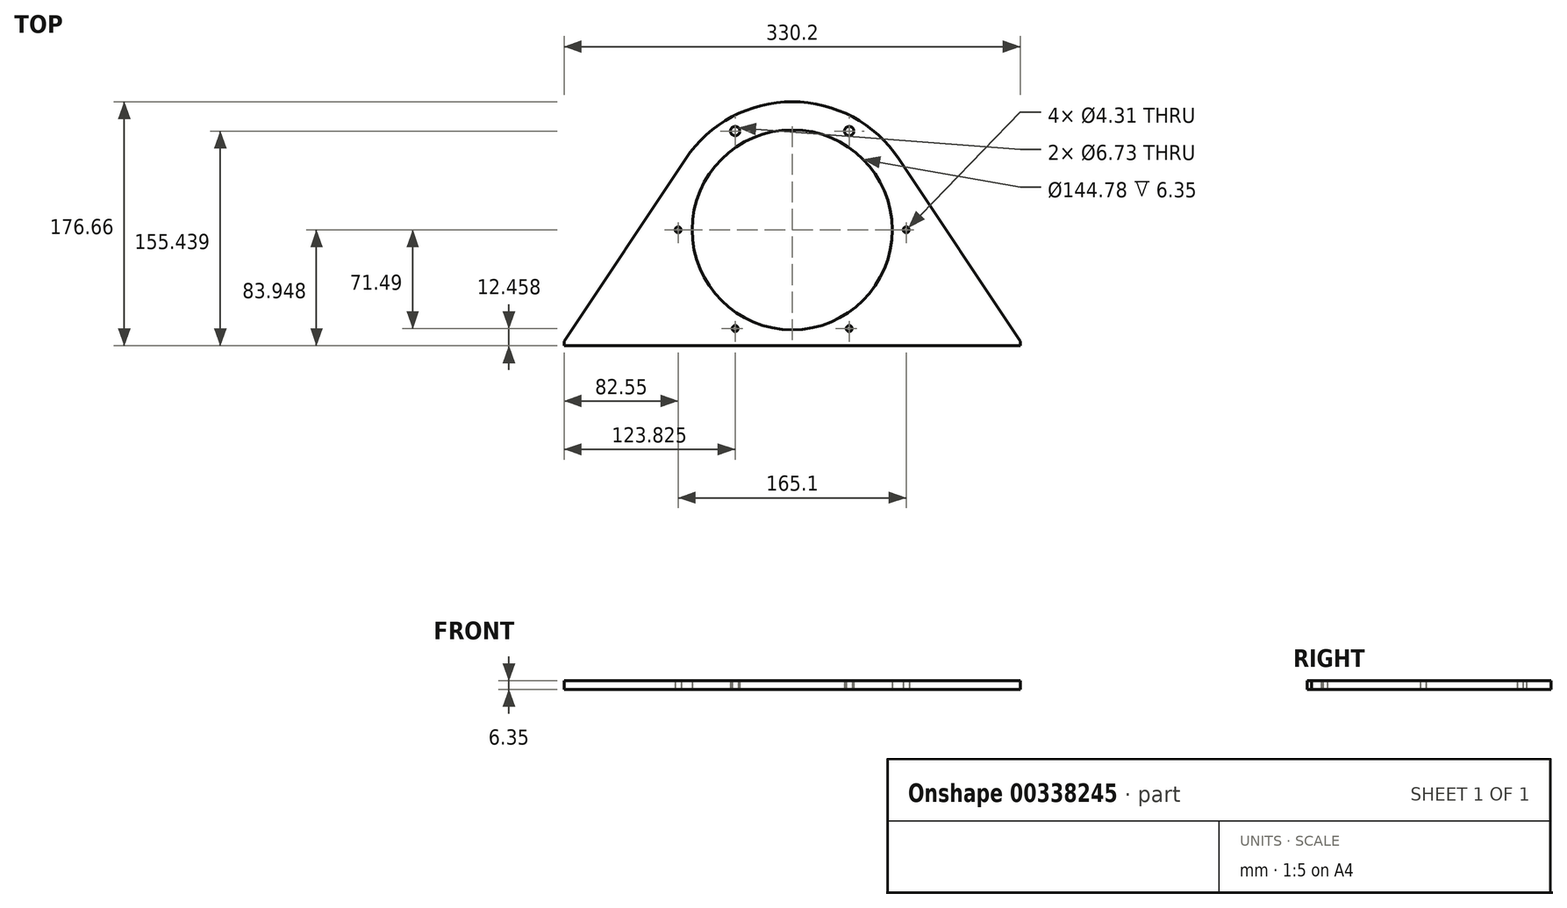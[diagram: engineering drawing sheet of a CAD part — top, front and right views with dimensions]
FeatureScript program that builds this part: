
annotation { "Feature Type Name" : "Feature", "Feature Type Description" : "" }
export const myFeature = defineFeature(function(context is Context, id is Id, definition is map)
    precondition{}
    {
        {
            var Q0;
            Q0=qCreatedBy(makeId("Top.planeOp"),FACE);
            var sketch = newSketch(context, id + "F0", { "sketchPlane" : qUnion([Q0])});
            skLineSegment(sketch, "E0", {"start": v(0, 0) * mm, "end": v(330.2, 0) * mm});
            skLineSegment(sketch, "E1", {"start": v(330.2, 0) * mm, "end": v(330.2, 3.17) * mm});
            skLineSegment(sketch, "E2", {"start": v(330.2, 3.17) * mm, "end": v(242.29, 135.3) * mm});
            skLineSegment(sketch, "E3", {"start": v(165.1, 0) * mm, "end": v(165.1, 83.95) * mm, "construction": true});
            skCircle(sketch, "E4", {"center": v(165.1, 83.95) * mm, "radius": 72.4 * mm});
            skArc(sketch, "E5", {"start": v(242.29, 135.3) * mm, "mid": v(165.1, 176.66) * mm, "end": v(87.91, 135.3) * mm});
            skLineSegment(sketch, "E6", {"start": v(165.1, 83.95) * mm, "end": v(247.65, 83.95) * mm, "construction": true});
            skLineSegment(sketch, "E7", {"start": v(165.1, 83.95) * mm, "end": v(123.82, 155.44) * mm, "construction": true});
            skLineSegment(sketch, "E8", {"start": v(165.1, 83.95) * mm, "end": v(206.38, 155.44) * mm, "construction": true});
            skLineSegment(sketch, "E9", {"start": v(165.1, 83.95) * mm, "end": v(165.1, 155.44) * mm, "construction": true});
            skLineSegment(sketch, "E10", {"start": v(123.83, 155.44) * mm, "end": v(206.37, 155.44) * mm, "construction": true});
            skCircle(sketch, "E11", {"center": v(123.83, 155.44) * mm, "radius": 10.16 * mm, "construction": true});
            skLineSegment(sketch, "E12", {"start": v(0, 0) * mm, "end": v(0, 3.17) * mm});
            skLineSegment(sketch, "E13", {"start": v(0, 3.17) * mm, "end": v(87.91, 135.3) * mm});
            skLineSegment(sketch, "E14", {"start": v(165.1, 83.95) * mm, "end": v(206.37, 12.46) * mm, "construction": true});
            skLineSegment(sketch, "E15", {"start": v(206.37, 12.46) * mm, "end": v(247.65, 83.95) * mm, "construction": true});
            skLineSegment(sketch, "E16", {"start": v(247.65, 83.95) * mm, "end": v(206.38, 155.44) * mm, "construction": true});
            skLineSegment(sketch, "E17", {"start": v(123.83, 155.44) * mm, "end": v(82.55, 83.95) * mm, "construction": true});
            skLineSegment(sketch, "E18", {"start": v(82.55, 83.95) * mm, "end": v(165.1, 83.95) * mm, "construction": true});
            skLineSegment(sketch, "E19", {"start": v(165.1, 83.95) * mm, "end": v(123.83, 12.46) * mm, "construction": true});
            skLineSegment(sketch, "E20", {"start": v(123.83, 12.46) * mm, "end": v(82.55, 83.95) * mm, "construction": true});
            skCircle(sketch, "E21", {"center": v(123.83, 155.44) * mm, "radius": 3.37 * mm});
            skCircle(sketch, "E22", {"center": v(206.37, 155.44) * mm, "radius": 3.37 * mm});
            skCircle(sketch, "E23", {"center": v(82.55, 83.95) * mm, "radius": 2.15 * mm});
            skCircle(sketch, "E24", {"center": v(123.83, 12.46) * mm, "radius": 2.15 * mm});
            skCircle(sketch, "E25", {"center": v(206.37, 12.46) * mm, "radius": 2.15 * mm});
            skCircle(sketch, "E26", {"center": v(247.65, 83.95) * mm, "radius": 2.15 * mm});
            skSolve(sketch);
        }
        {
            var Q0;
            Q0=qSketchRegion(id+"F0",true);
            extrude(context, id + "F1", {"entities" : qUnion([Q0]), "depth" : 6.35 * mm});
        }
    });
